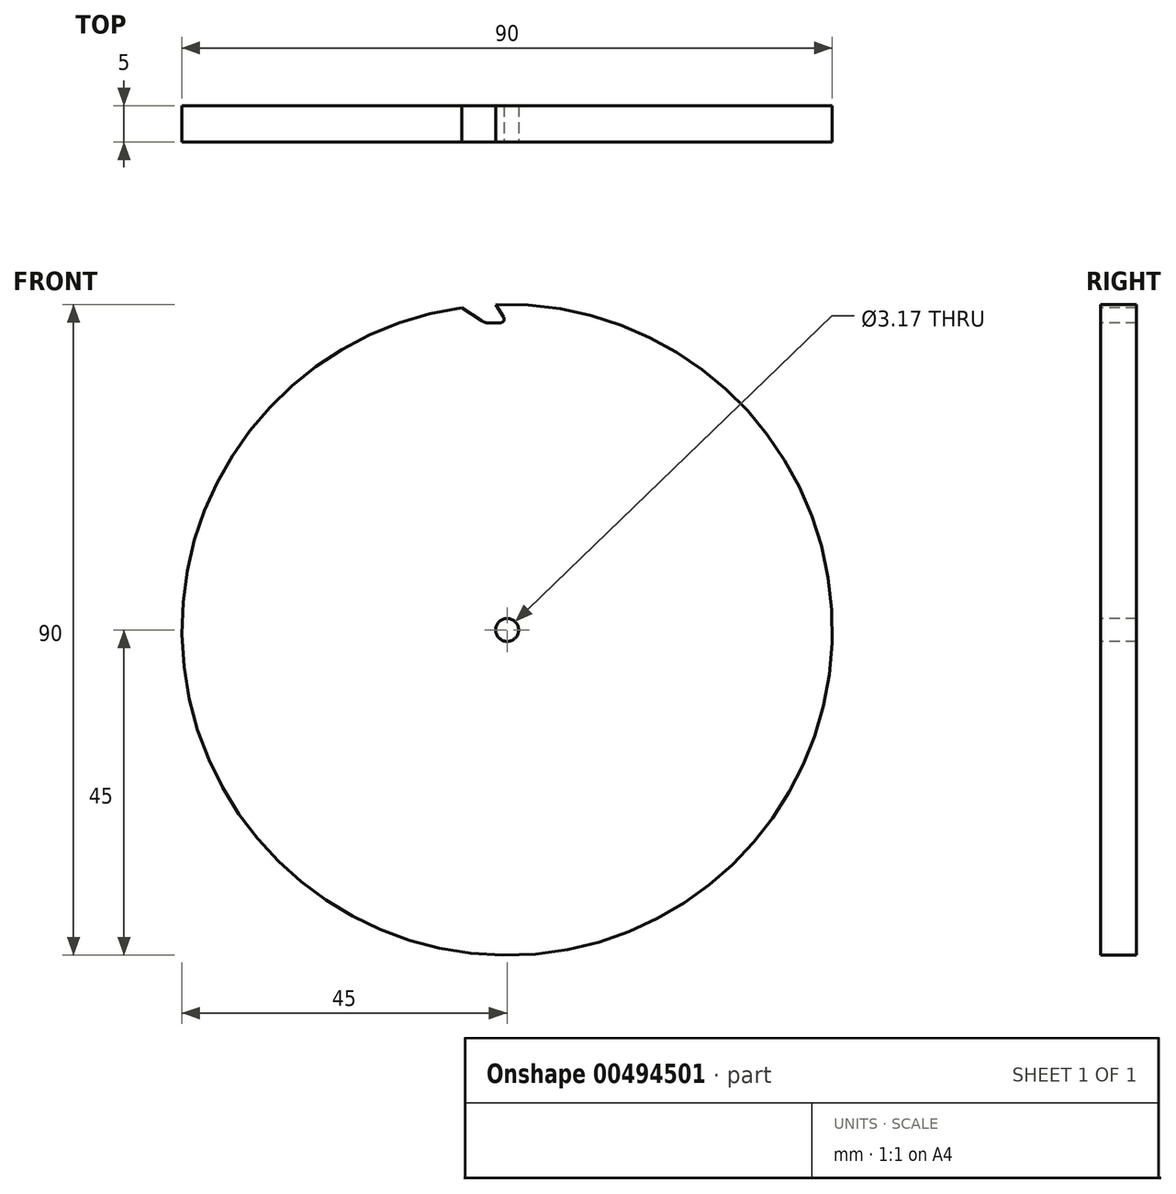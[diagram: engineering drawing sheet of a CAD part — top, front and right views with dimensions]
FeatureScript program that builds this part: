
annotation { "Feature Type Name" : "Feature", "Feature Type Description" : "" }
export const myFeature = defineFeature(function(context is Context, id is Id, definition is map)
    precondition{}
    {
        {
            var Q0;
            Q0=qCreatedBy(makeId("Front.planeOp"),FACE);
            var sketch = newSketch(context, id + "F0", { "sketchPlane" : qUnion([Q0])});
            skCircle(sketch, "E0", {"center": v(0, 0) * mm, "radius": 45 * mm});
            skSolve(sketch);
        }
        {
            var Q0;
            Q0=qSketchRegion(id+"F0",true);
            extrude(context, id + "F1", {"entities" : qUnion([Q0]), "depth" : 5 * mm, "offsetDistance" : 25 * mm});
        }
        {
            var Q0;
            Q0=makeQuery(id+"F1.opExtrude","CAP_FACE",FACE,{"disambiguationData":[OSD([sQuery(id+"F0.wireOp",EDGE,"E0")])],"isStart":false});
            var sketch = newSketch(context, id + "F2", { "sketchPlane" : qUnion([Q0])});
            skCircle(sketch, "E1", {"center": v(0, 0) * mm, "radius": 42.5 * mm});
            skLineSegment(sketch, "E2", {"start": v(0, 42.5) * mm, "end": v(-1.57, 44.97) * mm});
            skLineSegment(sketch, "E3", {"start": v(0.52, 45) * mm, "end": v(2.96, 42.4) * mm});
            skLineSegment(sketch, "E4", {"start": v(0, 42.5) * mm, "end": v(0, 0) * mm, "construction": true});
            skLineSegment(sketch, "E5", {"start": v(0, 0) * mm, "end": v(2.96, 42.4) * mm, "construction": true});
            skLineSegment(sketch, "E6", {"start": v(-2.96, 42.4) * mm, "end": v(-6.26, 44.56) * mm});
            skLineSegment(sketch, "E7", {"start": v(-1.57, 44.97) * mm, "end": v(0, 0) * mm, "construction": true});
            skLineSegment(sketch, "E8", {"start": v(0.52, 45) * mm, "end": v(0, 0) * mm, "construction": true});
            skLineSegment(sketch, "E9", {"start": v(-6.26, 44.56) * mm, "end": v(0, 0) * mm, "construction": true});
            skLineSegment(sketch, "E10", {"start": v(-2.96, 42.4) * mm, "end": v(0, 0) * mm, "construction": true});
            skSolve(sketch);
        }
        {
            var Q0;
            Q0=makeQuery(id+"F1.opExtrude","CAP_FACE",FACE,{"disambiguationData":[OSD([sQuery(id+"F0.wireOp",EDGE,"E0")])],"isStart":false});
            var sketch = newSketch(context, id + "F3", { "sketchPlane" : qUnion([Q0])});
            skCircle(sketch, "E11", {"center": v(0, 0) * mm, "radius": 22.93 * mm});
            skSolve(sketch);
        }
        {
            var Q0;
            {var subQ0=sQuery(id+"F2.wireOp",EDGE,"E2");Q0=makeQuery(id+"F2.imprint","IMPRINT",FACE,{"disambiguationData":[TD([[makeQuery(id+"F2.imprint","IMPRINT",EDGE,{"derivedFrom":subQ0}),1.0]])]});}
            extrude(context, id + "F4", {"entities" : qUnion([Q0]), "operationType" : NewBodyOperationType.REMOVE, "oppositeDirection" : true, "depth" : 25 * mm, "offsetDistance" : 25 * mm});
        }
        {
            var Q0;
            Q0=makeQuery(id+"F4.boolean.opBoolean","COPY",EDGE,{"derivedFrom":makeQuery(id+"F4.opExtrude","SWEPT_EDGE",EDGE,{"disambiguationData":[OSD([sQuery(id+"F0.wireOp",EDGE,"E0"),sQuery(id+"F2.wireOp",EDGE,"E6")])]})});
            var Q1;
            Q1=makeQuery(id+"F4.boolean.opBoolean","COPY",EDGE,{"derivedFrom":makeQuery(id+"F4.opExtrude","SWEPT_EDGE",EDGE,{"disambiguationData":[OSD([sQuery(id+"F2.wireOp",EDGE,"E1"),sQuery(id+"F2.wireOp",EDGE,"E6")])]})});
            fillet(context, id + "F5", {"entities" : qUnion([Q0, Q1]), "radius" : 2 * mm, "tangentPropagation" : true, "allowEdgeOverflow" : false});
        }
        {
            var Q0;
            Q0=makeQuery(id+"F4.boolean.opBoolean","COPY",EDGE,{"derivedFrom":makeQuery(id+"F4.opExtrude","SWEPT_EDGE",EDGE,{"disambiguationData":[OSD([sQuery(id+"F2.wireOp",EDGE,"E1"),sQuery(id+"F2.wireOp",EDGE,"E2")])]})});
            fillet(context, id + "F6", {"entities" : qUnion([Q0]), "radius" : 0.5 * mm, "tangentPropagation" : true, "allowEdgeOverflow" : false});
        }
        {
            var Q0;
            Q0=makeQuery(id+"F1.opExtrude","CAP_FACE",FACE,{"disambiguationData":[OSD([sQuery(id+"F0.wireOp",EDGE,"E0")])],"isStart":false});
            var sketch = newSketch(context, id + "F7", { "sketchPlane" : qUnion([Q0])});
            skCircle(sketch, "E12", {"center": v(0, 0) * mm, "radius": 1.59 * mm});
            skSolve(sketch);
        }
        {
            var Q0;
            Q0=qSketchRegion(id+"F7",true);
            extrude(context, id + "F8", {"entities" : qUnion([Q0]), "operationType" : NewBodyOperationType.REMOVE, "oppositeDirection" : true, "depth" : 25 * mm, "offsetDistance" : 25 * mm});
        }
    });
